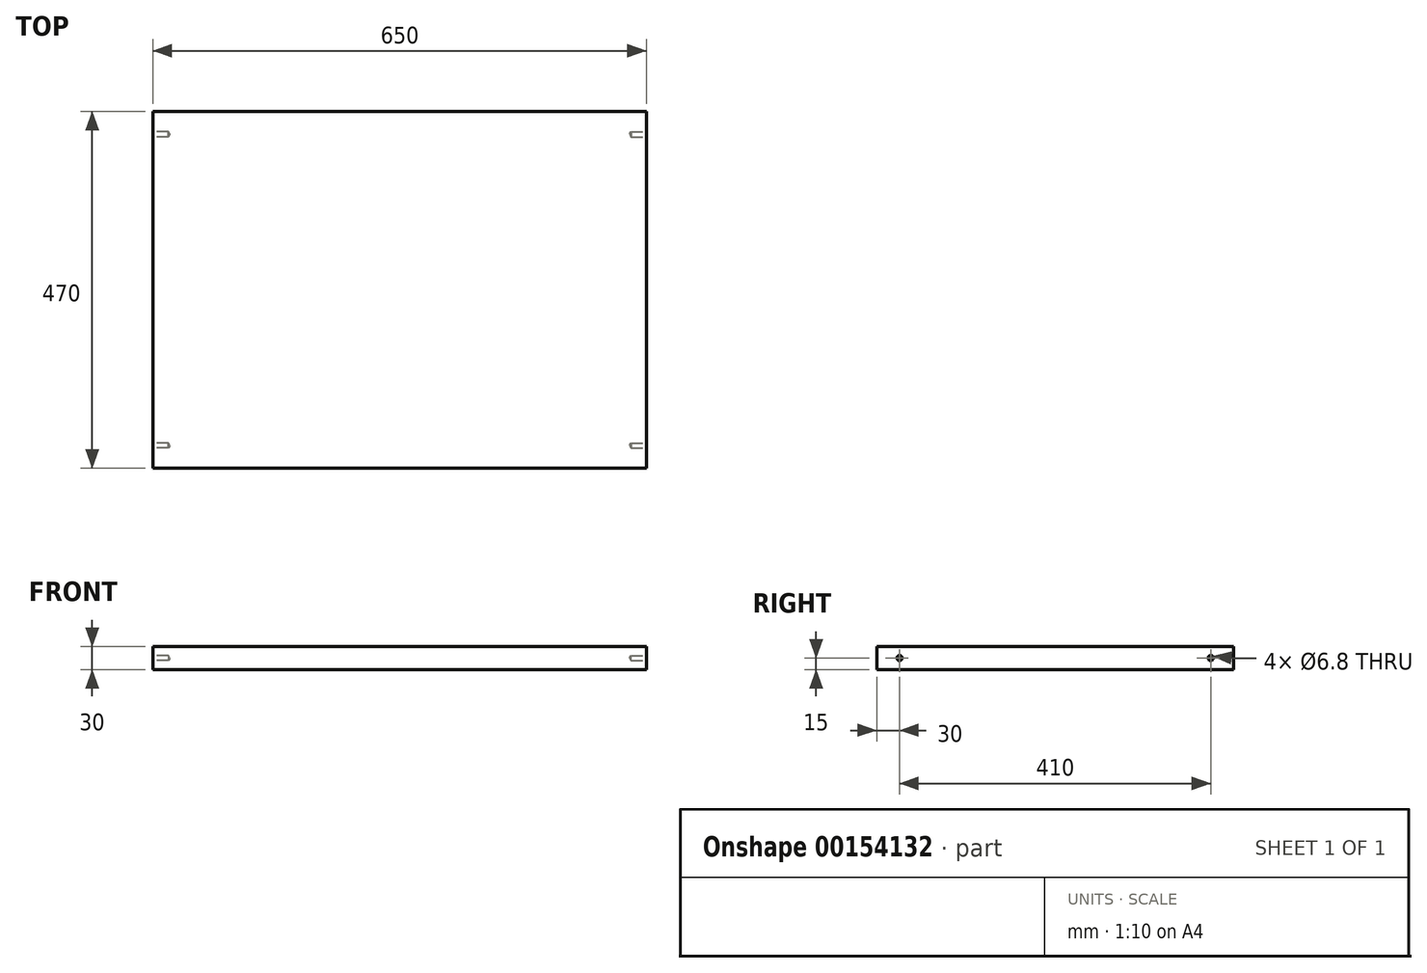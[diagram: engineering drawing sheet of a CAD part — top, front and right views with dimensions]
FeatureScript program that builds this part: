
annotation { "Feature Type Name" : "Feature", "Feature Type Description" : "" }
export const myFeature = defineFeature(function(context is Context, id is Id, definition is map)
    precondition{}
    {
        {
            var Q0;
            Q0=qCreatedBy(makeId("Top.planeOp"),FACE);
            var sketch = newSketch(context, id + "F0", { "sketchPlane" : qUnion([Q0])});
            skLineSegment(sketch, "E0.bottom", {"start": v(325, -235) * mm, "end": v(-325, -235) * mm});
            skLineSegment(sketch, "E0.top", {"start": v(325, 235) * mm, "end": v(-325, 235) * mm});
            skLineSegment(sketch, "E0.left", {"start": v(325, -235) * mm, "end": v(325, 235) * mm});
            skLineSegment(sketch, "E0.right", {"start": v(-325, -235) * mm, "end": v(-325, 235) * mm});
            skPoint(sketch, "E0.middle", {"position": v(0, 0) * mm});
            skSolve(sketch);
        }
        {
            var Q0;
            Q0 = qSketchRegion(id + "F0", true);
            extrude(context, id + "F1", {"entities" : qUnion([Q0]), "depth" : 30 * mm});
        }
        {
            var Q0;
            Q0=makeQuery(id+"F1.opExtrude","SWEPT_FACE",FACE,{"disambiguationData":[OSD([sQuery(id+"F0.wireOp",EDGE,"E0.left")])]});
            var sketch = newSketch(context, id + "F2", { "sketchPlane" : qUnion([Q0])});
            skLineSegment(sketch, "E1.bottom", {"start": v(-235, 0) * mm, "end": v(235, 0) * mm});
            skLineSegment(sketch, "E1.top", {"start": v(-235, 30) * mm, "end": v(235, 30) * mm});
            skLineSegment(sketch, "E1.left", {"start": v(-235, 0) * mm, "end": v(-235, 30) * mm});
            skLineSegment(sketch, "E1.right", {"start": v(235, 0) * mm, "end": v(235, 30) * mm});
            skPoint(sketch, "E2", {"position": v(-205, 15) * mm});
            skPoint(sketch, "E3", {"position": v(205, 15) * mm});
            skSolve(sketch);
        }
        {
            var Q0;
            Q0=makeQuery(id+"F1.opExtrude","SWEPT_FACE",FACE,{"disambiguationData":[OSD([sQuery(id+"F0.wireOp",EDGE,"E0.right")])]});
            var sketch = newSketch(context, id + "F3", { "sketchPlane" : qUnion([Q0])});
            skLineSegment(sketch, "E4.bottom", {"start": v(-235, 0) * mm, "end": v(235, 0) * mm});
            skLineSegment(sketch, "E4.top", {"start": v(-235, 30) * mm, "end": v(235, 30) * mm});
            skLineSegment(sketch, "E4.left", {"start": v(-235, 0) * mm, "end": v(-235, 30) * mm});
            skLineSegment(sketch, "E4.right", {"start": v(235, 0) * mm, "end": v(235, 30) * mm});
            skPoint(sketch, "E5", {"position": v(-205, 15) * mm});
            skPoint(sketch, "E6", {"position": v(205, 15) * mm});
            skSolve(sketch);
        }
        {
            var Q0;
            Q0=sQuery(id+"F2.wireOp",VERTEX,"E2");
            var Q1;
            Q1=sQuery(id+"F2.wireOp",VERTEX,"E3");
            var Q2;
            Q2=sQuery(id+"F3.wireOp",VERTEX,"E5");
            var Q3;
            Q3=sQuery(id+"F3.wireOp",VERTEX,"E6");
            var Q4;
            Q4=makeQuery(id+"F1.opExtrude","SWEPT_BODY",BODY,{"disambiguationData":[OSD([sQuery(id+"F0.wireOp",EDGE,"E0.bottom"),sQuery(id+"F0.wireOp",EDGE,"E0.top"),sQuery(id+"F0.wireOp",EDGE,"E0.left"),sQuery(id+"F0.wireOp",EDGE,"E0.right")])]});
            hole(context, id + "F4", {"style" : HoleStyle.SIMPLE, "endStyle" : HoleEndStyle.BLIND, "standardTappedOrClearance" : lookupTablePath({ "standard" : "ISO", "engagement" : "75%", "pitch" : "1.25 mm", "size" : "M8", "type" : "Tapped" }), "standardBlindInLast" : lookupTablePath({ "standard" : "ISO", "engagement" : "75%", "pitch" : "1.25 mm", "size" : "M8", "type" : "Tapped" }), "holeDiameter" : 6.8 * mm, "holeDepth" : 20 * mm, "locations" : qUnion([Q0, Q1, Q2, Q3]), "scope" : qUnion([Q4]), "majorDiameter" : 8 * mm});
        }
    });
